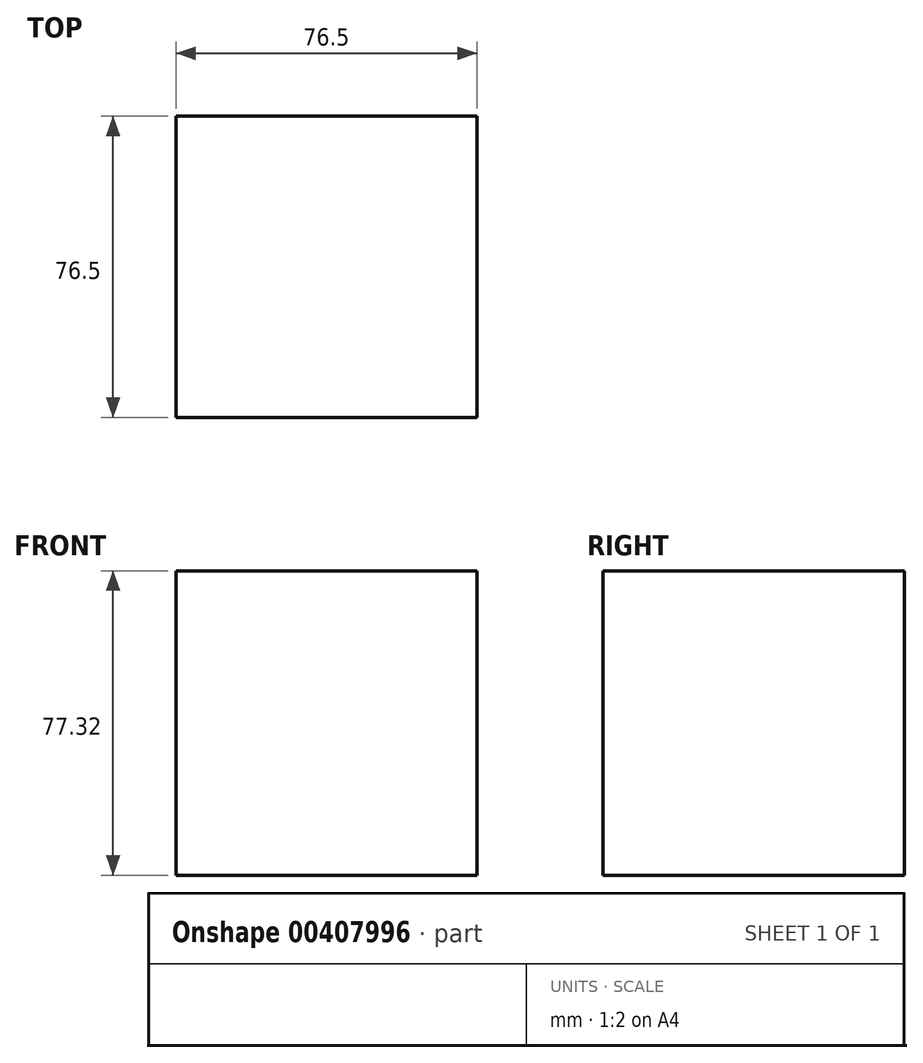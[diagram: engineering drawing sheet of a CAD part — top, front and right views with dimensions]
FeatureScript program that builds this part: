
annotation { "Feature Type Name" : "Feature", "Feature Type Description" : "" }
export const myFeature = defineFeature(function(context is Context, id is Id, definition is map)
    precondition{}
    {
        {
            var Q0;
            Q0=qCreatedBy(makeId("Top.planeOp"),FACE);
            var sketch = newSketch(context, id + "F0", { "sketchPlane" : qUnion([Q0])});
            skLineSegment(sketch, "E0.bottom", {"start": v(0, 0) * mm, "end": v(76.5, 0) * mm});
            skLineSegment(sketch, "E0.top", {"start": v(0, 76.5) * mm, "end": v(76.5, 76.5) * mm});
            skLineSegment(sketch, "E0.left", {"start": v(0, 0) * mm, "end": v(0, 76.5) * mm});
            skLineSegment(sketch, "E0.right", {"start": v(76.5, 0) * mm, "end": v(76.5, 76.5) * mm});
            skSolve(sketch);
        }
        {
            var Q0;
            Q0=makeQuery(id+"F0.imprint","IMPRINT",FACE,{"disambiguationData":[TD([[makeQuery(id+"F0.imprint","IMPRINT",EDGE,{"derivedFrom":sQuery(id+"F0.wireOp",EDGE,"E0.bottom")}),1.0]])]});
            extrude(context, id + "F1", {"entities" : qUnion([Q0]), "depth" : 77.32 * mm});
        }
    });
